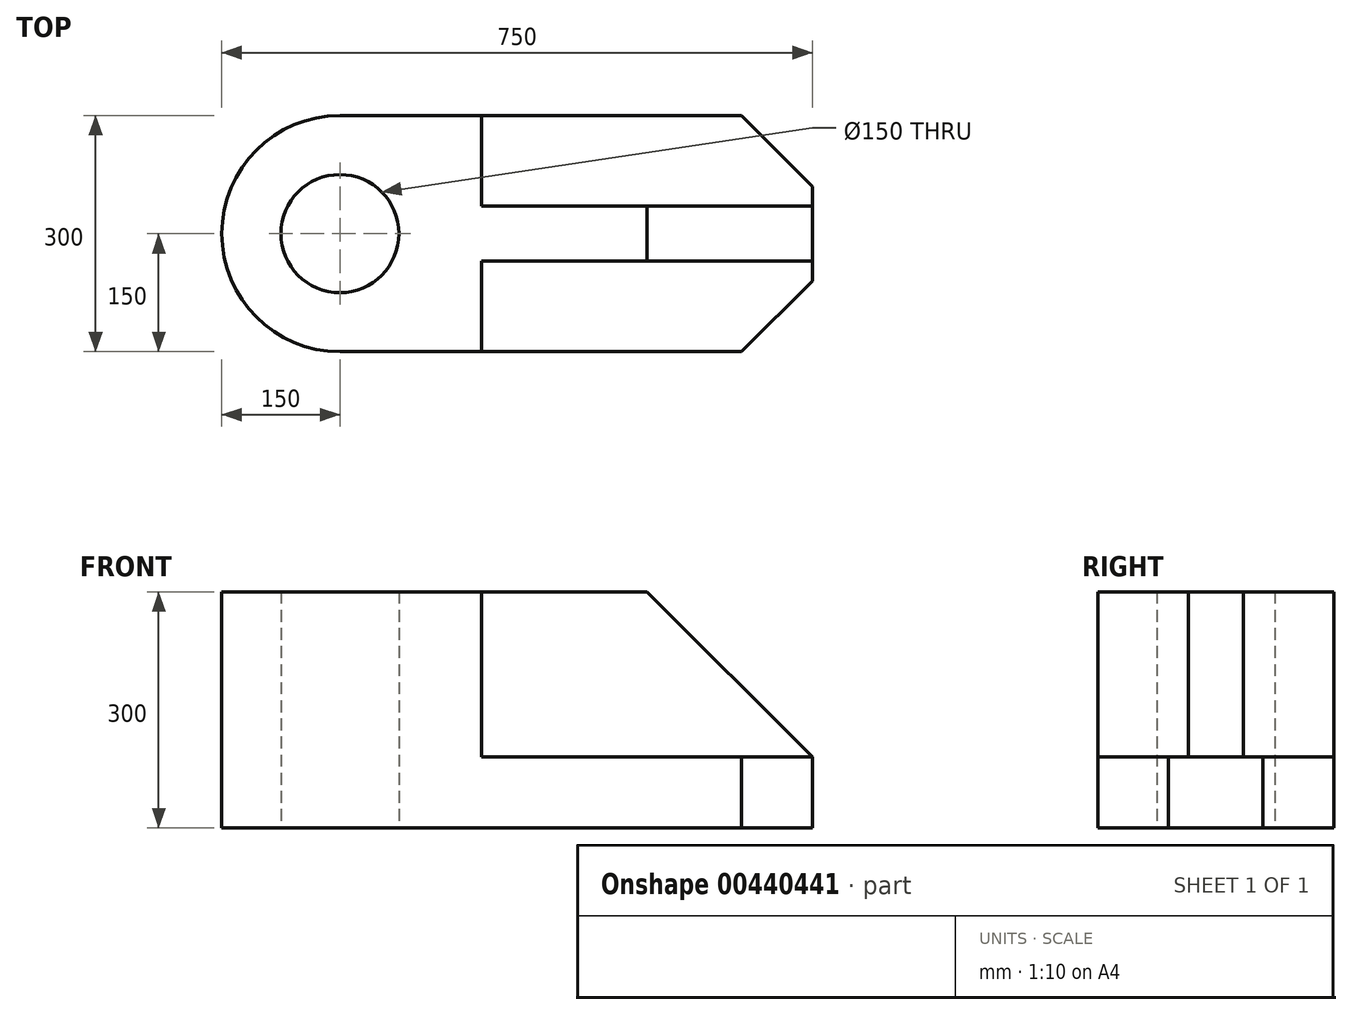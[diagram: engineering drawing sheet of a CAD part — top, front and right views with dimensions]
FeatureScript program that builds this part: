
annotation { "Feature Type Name" : "Feature", "Feature Type Description" : "" }
export const myFeature = defineFeature(function(context is Context, id is Id, definition is map)
    precondition{}
    {
        {
            var Q0;
            Q0=qCreatedBy(makeId("Top.planeOp"),FACE);
            var sketch = newSketch(context, id + "F0", { "sketchPlane" : qUnion([Q0])});
            skLineSegment(sketch, "E0", {"start": v(0, 0) * mm, "end": v(-510, 0) * mm});
            skLineSegment(sketch, "E1", {"start": v(0, 300) * mm, "end": v(-510, 300) * mm});
            skArc(sketch, "E2", {"start": v(-510, 300) * mm, "mid": v(-660, 150) * mm, "end": v(-510, 0) * mm});
            skLineSegment(sketch, "E3", {"start": v(90, 90) * mm, "end": v(90, 210) * mm});
            skLineSegment(sketch, "E4", {"start": v(0, 300) * mm, "end": v(90, 210) * mm});
            skLineSegment(sketch, "E5", {"start": v(90, 90) * mm, "end": v(0, 0) * mm});
            skLineSegment(sketch, "E6", {"start": v(-510, 300) * mm, "end": v(-330, 300) * mm});
            skCircle(sketch, "E7", {"center": v(-510, 150) * mm, "radius": 75 * mm});
            skSolve(sketch);
        }
        {
            var Q0;
            Q0=makeQuery(id+"F0.imprint","IMPRINT",FACE,{"disambiguationData":[TD([[makeQuery(id+"F0.imprint","IMPRINT",EDGE,{"derivedFrom":sQuery(id+"F0.wireOp",EDGE,"E0")}),-1.0]])]});
            extrude(context, id + "F1", {"entities" : qUnion([Q0]), "depth" : 90 * mm});
        }
        {
            var Q0;
            Q0=makeQuery(id+"F1.opExtrude","CAP_FACE",FACE,{"disambiguationData":[OSD([sQuery(id+"F0.wireOp",EDGE,"E0"),sQuery(id+"F0.wireOp",EDGE,"E1"),sQuery(id+"F0.wireOp",EDGE,"E2"),sQuery(id+"F0.wireOp",EDGE,"E3"),sQuery(id+"F0.wireOp",EDGE,"E4"),sQuery(id+"F0.wireOp",EDGE,"E5"),sQuery(id+"F0.wireOp",EDGE,"E6"),sQuery(id+"F0.wireOp",EDGE,"E7")])],"isStart":false});
            var sketch = newSketch(context, id + "F2", { "sketchPlane" : qUnion([Q0])});
            skLineSegment(sketch, "E8", {"start": v(-510, 300) * mm, "end": v(-330, 300) * mm});
            skLineSegment(sketch, "E9", {"start": v(-330, 0) * mm, "end": v(-510, 0) * mm});
            skArc(sketch, "E10", {"start": v(-510, 300) * mm, "mid": v(-660, 150) * mm, "end": v(-510, 0) * mm});
            skLineSegment(sketch, "E11", {"start": v(-330, 300) * mm, "end": v(-330, 185) * mm});
            skLineSegment(sketch, "E12", {"start": v(-330, 185) * mm, "end": v(90, 185) * mm});
            skLineSegment(sketch, "E13", {"start": v(-330, 0) * mm, "end": v(-330, 115) * mm});
            skLineSegment(sketch, "E14", {"start": v(-330, 115) * mm, "end": v(90, 115) * mm});
            skLineSegment(sketch, "E15", {"start": v(-330, 185) * mm, "end": v(-330, 115) * mm});
            skSolve(sketch);
        }
        {
            var Q0;
            Q0=makeQuery(id+"F2.imprint","IMPRINT",FACE,{"disambiguationData":[TD([[makeQuery(id+"F2.imprint","IMPRINT",EDGE,{"derivedFrom":sQuery(id+"F2.wireOp",EDGE,"E8")}),1.0]])]});
            var Q1;
            {var subQ0=sQuery(id+"F2.wireOp",EDGE,"E12");Q1=makeQuery(id+"F2.imprint","IMPRINT",FACE,{"disambiguationData":[TD([[makeQuery(id+"F2.imprint","IMPRINT",EDGE,{"derivedFrom":subQ0}),-1.0]])]});}
            extrude(context, id + "F3", {"entities" : qUnion([Q0, Q1]), "operationType" : NewBodyOperationType.ADD, "depth" : 210 * mm});
        }
        {
            var Q0;
            Q0=makeQuery(id+"F3.opExtrude","CAP_EDGE",EDGE,{"disambiguationData":[OSD([sQuery(id+"F0.wireOp",EDGE,"E3")])],"isStart":false});
            chamfer(context, id + "F4", {"entities" : qUnion([Q0]), "width" : 210 * mm, "tangentPropagation" : true});
        }
    });
